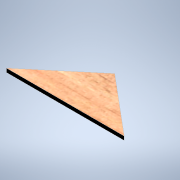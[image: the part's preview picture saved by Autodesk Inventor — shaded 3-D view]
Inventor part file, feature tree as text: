
AUTODESK INVENTOR PART (.ipt)
format: ipt  version: 2021 (Build 250183000, 183)  size: 111,616 bytes
history: native  units: mm
features: extrude x1, sketch x1
ambient origin geometry x8: Origin, YZ Plane, XZ Plane, XY Plane, X Axis, Y Axis, Z Axis, Center Point
bodies: Volumenkörper1 (feature_tree)
feature tree (2):
  extrude  "Extrusion1"  Depth=3.0mm TaperAngle=0.0deg
  sketch  "Skizze1"  dims[d0=93.0mm d2=3.0mm d3=0.0mm d4=39.0mm]
